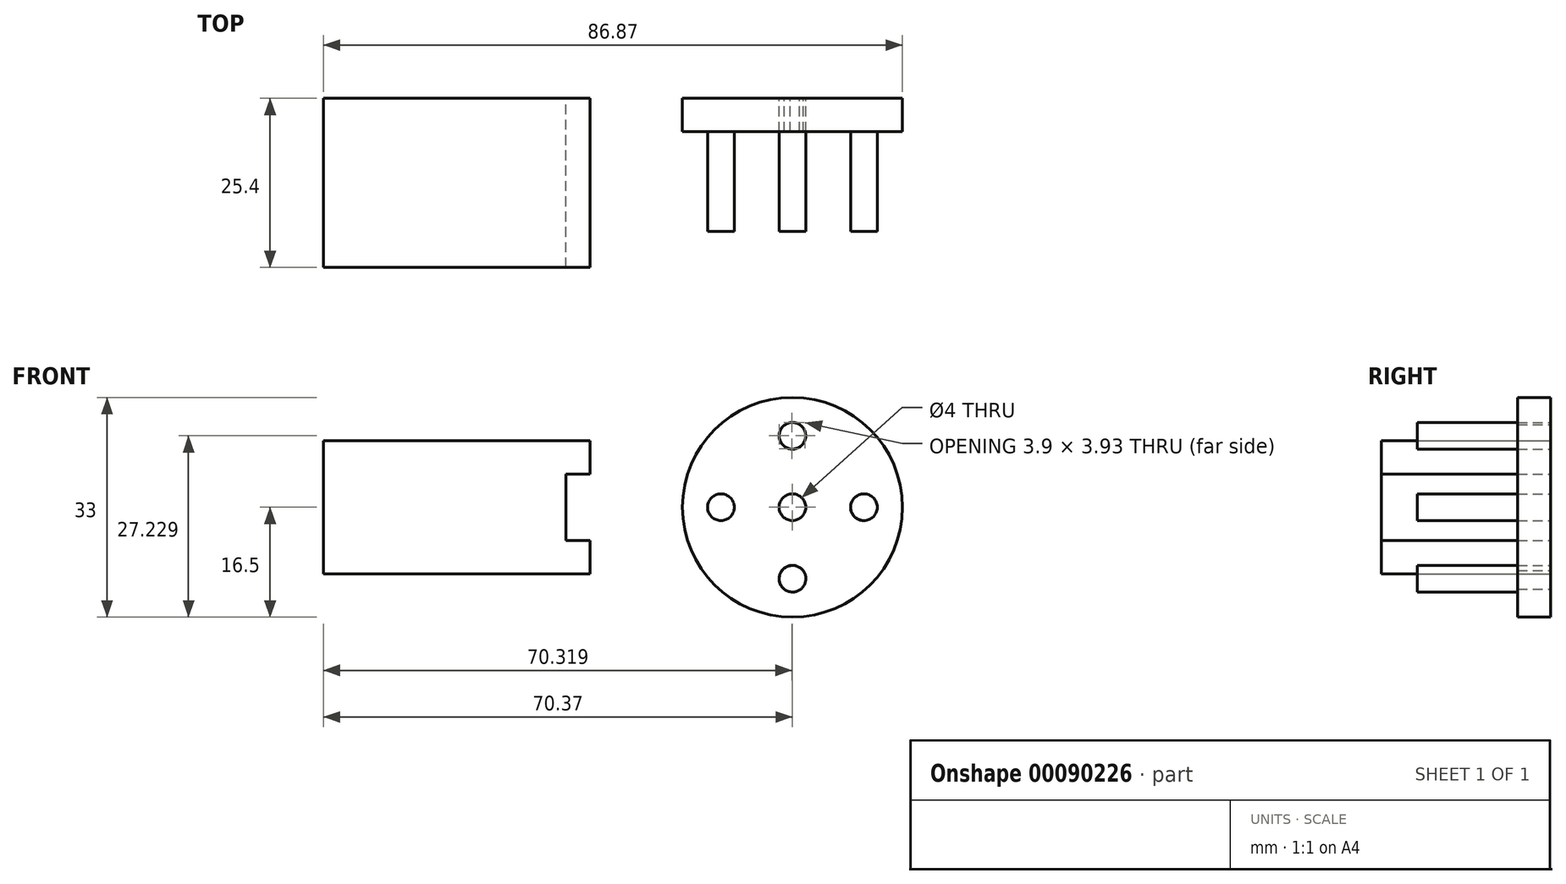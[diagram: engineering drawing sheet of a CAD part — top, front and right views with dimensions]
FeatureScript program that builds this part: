
annotation { "Feature Type Name" : "Feature", "Feature Type Description" : "" }
export const myFeature = defineFeature(function(context is Context, id is Id, definition is map)
    precondition{}
    {
        {
            var Q0;
            Q0=qCreatedBy(makeId("Front.planeOp"),FACE);
            var sketch = newSketch(context, id + "F0", { "sketchPlane" : qUnion([Q0])});
            skCircle(sketch, "E0", {"center": v(0, 0) * mm, "radius": 16.5 * mm});
            skCircle(sketch, "E1", {"center": v(0, 0) * mm, "radius": 2 * mm});
            skCircle(sketch, "E2", {"center": v(-10.72, 0) * mm, "radius": 2 * mm});
            skCircle(sketch, "E3.1.0", {"center": v(0, -10.72) * mm, "radius": 2 * mm});
            skCircle(sketch, "E3.2.0", {"center": v(10.72, 0) * mm, "radius": 2 * mm});
            skCircle(sketch, "E3.3.0", {"center": v(0, 10.72) * mm, "radius": 2 * mm});
            skSolve(sketch);
        }
        {
            var Q0;
            Q0 = qSketchRegion(id + "F0", true);
            extrude(context, id + "F1", {"entities" : qUnion([Q0]), "depth" : 5 * mm});
        }
        {
            var Q0;
            Q0=sQuery(id+"F0.wireOp",EDGE,"E3.3.0");
            extrude(context, id + "F2", {"bodyType" : ToolBodyType.SURFACE, "surfaceEntities" : qUnion([Q0]), "depth" : 20 * mm});
        }
        {
            var Q0;
            Q0=sQuery(id+"F0.wireOp",EDGE,"E2");
            extrude(context, id + "F3", {"bodyType" : ToolBodyType.SURFACE, "surfaceEntities" : qUnion([Q0]), "depth" : 20 * mm});
        }
        {
            var Q0;
            Q0=sQuery(id+"F0.wireOp",EDGE,"E3.2.0");
            extrude(context, id + "F4", {"bodyType" : ToolBodyType.SURFACE, "surfaceEntities" : qUnion([Q0]), "depth" : 20 * mm});
        }
        {
            var Q0;
            Q0=sQuery(id+"F0.wireOp",EDGE,"E3.1.0");
            extrude(context, id + "F5", {"bodyType" : ToolBodyType.SURFACE, "surfaceEntities" : qUnion([Q0]), "depth" : 20 * mm});
        }
        {
            var Q0;
            Q0=qCreatedBy(makeId("Front.planeOp"),FACE);
            var sketch = newSketch(context, id + "F6", { "sketchPlane" : qUnion([Q0])});
            skCircle(sketch, "E4", {"center": v(-10.73, 0) * mm, "radius": 2 * mm});
            skSolve(sketch);
        }
        {
            var Q0;
            Q0 = qSketchRegion(id + "F6", true);
            extrude(context, id + "F7", {"entities" : qUnion([Q0]), "operationType" : NewBodyOperationType.ADD, "depth" : 20 * mm});
        }
        {
            var Q0;
            Q0=qCreatedBy(makeId("Front.planeOp"),FACE);
            var sketch = newSketch(context, id + "F8", { "sketchPlane" : qUnion([Q0])});
            skCircle(sketch, "E5", {"center": v(0.02, -10.74) * mm, "radius": 2 * mm});
            skPoint(sketch, "E5.first.point", {"position": v(0, -8.74) * mm});
            skPoint(sketch, "E5.second.point", {"position": v(0, -12.74) * mm});
            skPoint(sketch, "E5.third.point", {"position": v(-1.58, -9.54) * mm});
            skSolve(sketch);
        }
        {
            var Q0;
            Q0=makeQuery(id+"F8.imprint","IMPRINT",FACE,{"disambiguationData":[TD([[makeQuery(id+"F8.imprint","IMPRINT",EDGE,{"derivedFrom":sQuery(id+"F8.wireOp",EDGE,"E5")}),1.0]])]});
            extrude(context, id + "F9", {"entities" : qUnion([Q0]), "operationType" : NewBodyOperationType.ADD, "depth" : 20 * mm});
        }
        {
            var Q0;
            Q0=qCreatedBy(makeId("Front.planeOp"),FACE);
            var sketch = newSketch(context, id + "F10", { "sketchPlane" : qUnion([Q0])});
            skCircle(sketch, "E6", {"center": v(10.73, 0) * mm, "radius": 2 * mm});
            skPoint(sketch, "E6.first.point", {"position": v(8.73, 0) * mm});
            skPoint(sketch, "E6.second.point", {"position": v(12.73, 0) * mm});
            skPoint(sketch, "E6.third.point", {"position": v(10.8, -2) * mm});
            skSolve(sketch);
        }
        {
            var Q0;
            Q0 = qSketchRegion(id + "F10", true);
            extrude(context, id + "F11", {"entities" : qUnion([Q0]), "operationType" : NewBodyOperationType.ADD, "depth" : 20 * mm});
        }
        {
            var Q0;
            Q0=qCreatedBy(makeId("Front.planeOp"),FACE);
            var sketch = newSketch(context, id + "F12", { "sketchPlane" : qUnion([Q0])});
            skCircle(sketch, "E7", {"center": v(0, 10.73) * mm, "radius": 2 * mm});
            skPoint(sketch, "E7.first.point", {"position": v(-2, 10.78) * mm});
            skPoint(sketch, "E7.second.point", {"position": v(2, 10.7) * mm});
            skPoint(sketch, "E7.third.point", {"position": v(0, 12.73) * mm});
            skSolve(sketch);
        }
        {
            var Q0;
            Q0 = qSketchRegion(id + "F12", true);
            extrude(context, id + "F13", {"entities" : qUnion([Q0]), "operationType" : NewBodyOperationType.ADD, "depth" : 20 * mm});
        }
        {
            var Q0;
            Q0=qCreatedBy(makeId("Front.planeOp"),FACE);
            var sketch = newSketch(context, id + "F14", { "sketchPlane" : qUnion([Q0])});
            skLineSegment(sketch, "E8.bottom", {"start": v(-30.37, -10) * mm, "end": v(-70.37, -10) * mm});
            skLineSegment(sketch, "E8.top", {"start": v(-30.37, 10) * mm, "end": v(-70.37, 10) * mm});
            skLineSegment(sketch, "E8.left", {"start": v(-30.37, -10) * mm, "end": v(-30.37, 10) * mm});
            skLineSegment(sketch, "E8.right", {"start": v(-70.37, -10) * mm, "end": v(-70.37, 10) * mm});
            skPoint(sketch, "E8.middle", {"position": v(-50.37, 0) * mm});
            skLineSegment(sketch, "E9.bottom", {"start": v(-33.96, 5) * mm, "end": v(-26.78, 5) * mm});
            skLineSegment(sketch, "E9.top", {"start": v(-33.96, -5) * mm, "end": v(-26.78, -5) * mm});
            skLineSegment(sketch, "E9.left", {"start": v(-33.96, 5) * mm, "end": v(-33.96, -5) * mm});
            skLineSegment(sketch, "E9.right", {"start": v(-26.78, 5) * mm, "end": v(-26.78, -5) * mm});
            skPoint(sketch, "E9.middle", {"position": v(-30.37, 0) * mm});
            skSolve(sketch);
        }
        {
            var Q0;
            {var subQ1=sQuery(id+"F14.wireOp",EDGE,"E8.bottom");Q0=makeQuery(id+"F14.imprint","IMPRINT",FACE,{"disambiguationData":[TD([[makeQuery(id+"F14.imprint","IMPRINT",EDGE,{"derivedFrom":subQ1}),-1.0]])]});}
            extrude(context, id + "F15", {"entities" : qUnion([Q0]), "depth" : 25.4 * mm});
        }
    });
